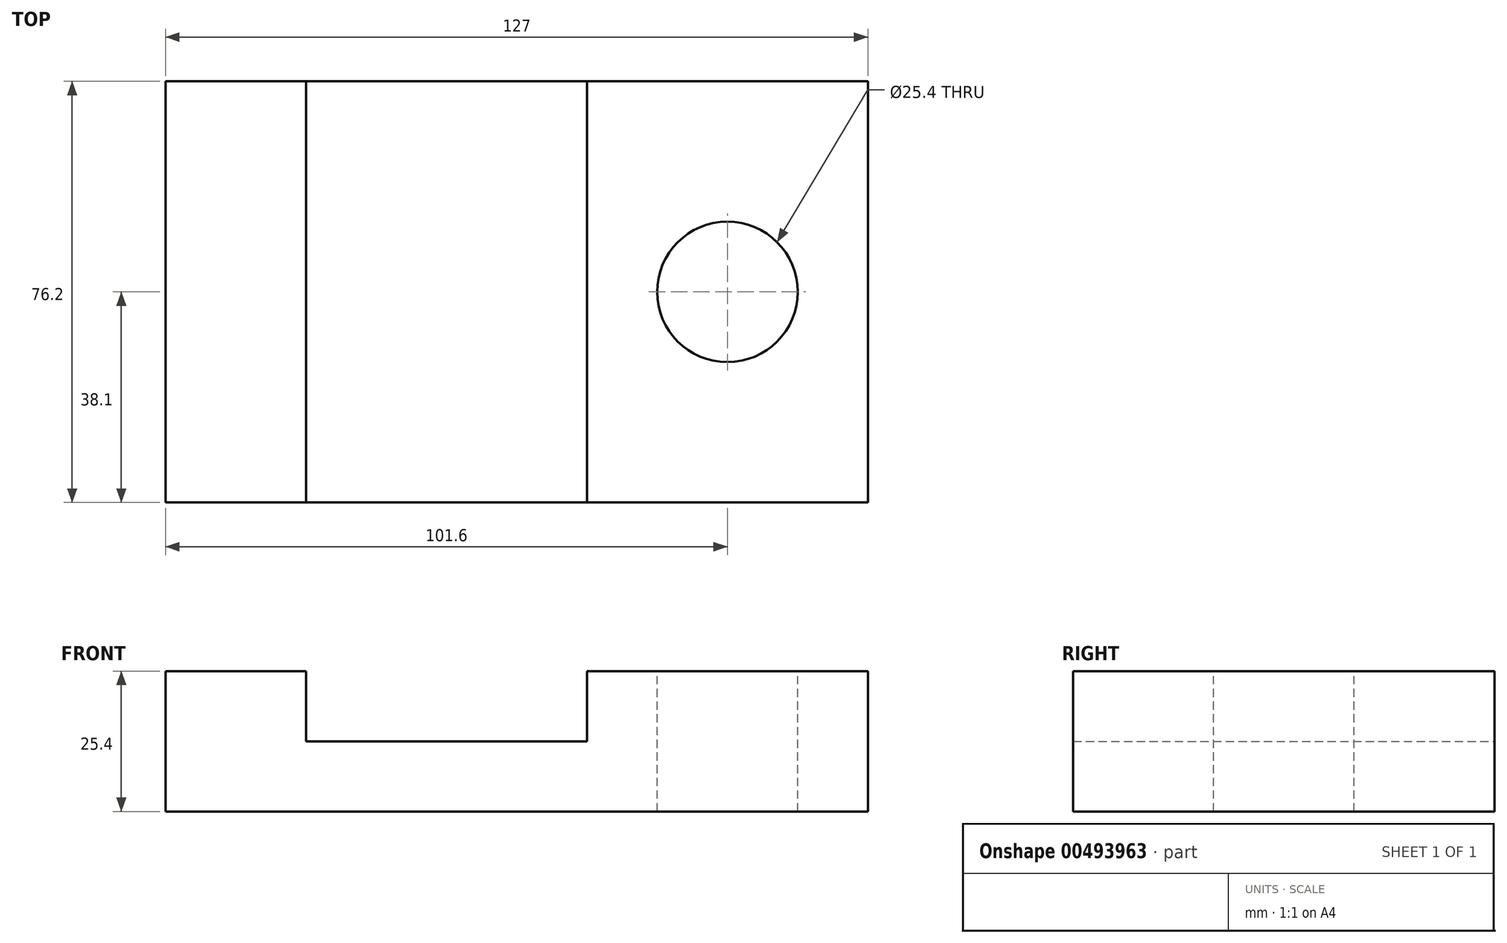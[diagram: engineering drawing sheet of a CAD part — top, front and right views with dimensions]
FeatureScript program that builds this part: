
annotation { "Feature Type Name" : "Feature", "Feature Type Description" : "" }
export const myFeature = defineFeature(function(context is Context, id is Id, definition is map)
    precondition{}
    {
        {
            var Q0;
            Q0=qCreatedBy(makeId("Front.planeOp"),FACE);
            var sketch = newSketch(context, id + "F0", { "sketchPlane" : qUnion([Q0])});
            skLineSegment(sketch, "E0", {"start": v(-76.2, 0) * mm, "end": v(-76.2, 25.4) * mm});
            skLineSegment(sketch, "E1", {"start": v(-76.2, 25.4) * mm, "end": v(-50.8, 25.4) * mm});
            skLineSegment(sketch, "E2", {"start": v(-50.8, 25.4) * mm, "end": v(-50.8, 12.7) * mm});
            skLineSegment(sketch, "E3", {"start": v(-50.8, 12.7) * mm, "end": v(0, 12.7) * mm});
            skLineSegment(sketch, "E4", {"start": v(0, 12.7) * mm, "end": v(0, 25.4) * mm});
            skLineSegment(sketch, "E5", {"start": v(0, 25.4) * mm, "end": v(50.8, 25.4) * mm});
            skLineSegment(sketch, "E6", {"start": v(50.8, 25.4) * mm, "end": v(50.8, 0) * mm});
            skLineSegment(sketch, "E7", {"start": v(50.8, 0) * mm, "end": v(-76.2, 0) * mm});
            skSolve(sketch);
        }
        {
            var Q0;
            Q0 = qSketchRegion(id + "F0", true);
            extrude(context, id + "F1", {"entities" : qUnion([Q0]), "depth" : 76.2 * mm});
        }
        {
            var Q0;
            Q0=makeQuery(id+"F1.opExtrude","SWEPT_FACE",FACE,{"disambiguationData":[OSD([sQuery(id+"F0.wireOp",EDGE,"E5")])]});
            var sketch = newSketch(context, id + "F2", { "sketchPlane" : qUnion([Q0])});
            skCircle(sketch, "E8", {"center": v(25.4, -38.1) * mm, "radius": 12.7 * mm});
            skSolve(sketch);
        }
        {
            var Q0;
            Q0=sQuery(id+"F2.wireOp",VERTEX,"E8.center");
            var Q1;
            Q1=makeQuery(id+"F1.opExtrude","SWEPT_BODY",BODY,{"disambiguationData":[OSD([sQuery(id+"F0.wireOp",EDGE,"E0"),sQuery(id+"F0.wireOp",EDGE,"E1"),sQuery(id+"F0.wireOp",EDGE,"E2"),sQuery(id+"F0.wireOp",EDGE,"E3"),sQuery(id+"F0.wireOp",EDGE,"E4"),sQuery(id+"F0.wireOp",EDGE,"E5"),sQuery(id+"F0.wireOp",EDGE,"E6"),sQuery(id+"F0.wireOp",EDGE,"E7")])]});
            hole(context, id + "F3", {"style" : HoleStyle.SIMPLE, "endStyle" : HoleEndStyle.THROUGH, "holeDiameter" : 25.4 * mm, "isTappedThrough" : true, "tappedDepth" : 12.7 * mm, "tapClearance" : 3, "locations" : qUnion([Q0]), "scope" : qUnion([Q1])});
        }
    });
